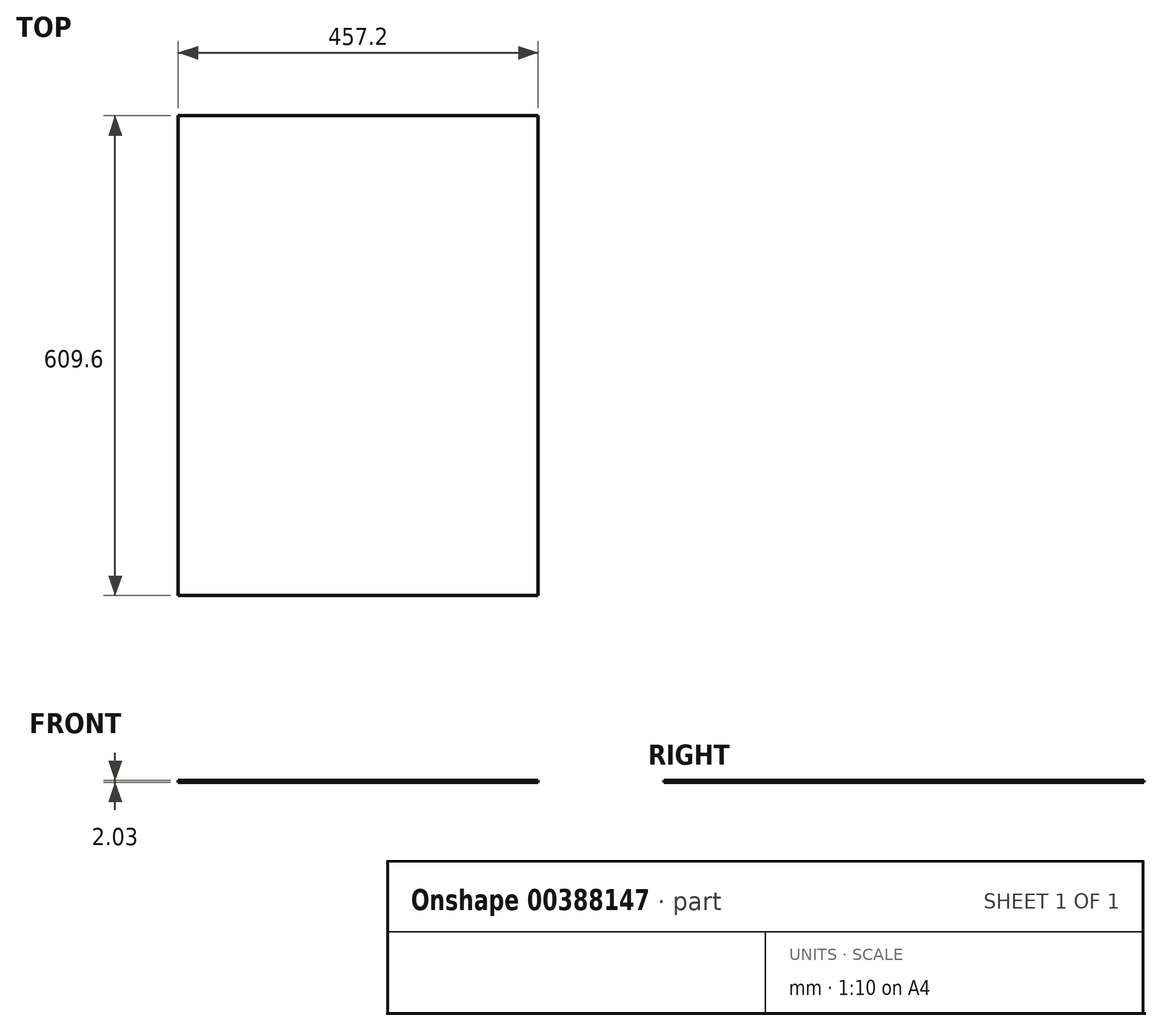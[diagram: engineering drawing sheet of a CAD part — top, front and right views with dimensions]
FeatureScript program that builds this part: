
annotation { "Feature Type Name" : "Feature", "Feature Type Description" : "" }
export const myFeature = defineFeature(function(context is Context, id is Id, definition is map)
    precondition{}
    {
        {
            var Q0;
            Q0=qCreatedBy(makeId("Top.planeOp"),FACE);
            var sketch = newSketch(context, id + "F0", { "sketchPlane" : qUnion([Q0])});
            skLineSegment(sketch, "E0.bottom", {"start": v(228.6, -304.8) * mm, "end": v(-228.6, -304.8) * mm});
            skLineSegment(sketch, "E0.top", {"start": v(228.6, 304.8) * mm, "end": v(-228.6, 304.8) * mm});
            skLineSegment(sketch, "E0.left", {"start": v(228.6, -304.8) * mm, "end": v(228.6, 304.8) * mm});
            skLineSegment(sketch, "E0.right", {"start": v(-228.6, -304.8) * mm, "end": v(-228.6, 304.8) * mm});
            skPoint(sketch, "E0.middle", {"position": v(0, 0) * mm});
            skLineSegment(sketch, "E1", {"start": v(228.6, 120.65) * mm, "end": v(-228.6, 120.65) * mm, "construction": true});
            skLineSegment(sketch, "E2", {"start": v(-228.6, -31.75) * mm, "end": v(228.6, -31.75) * mm, "construction": true});
            skSolve(sketch);
        }
        {
            var Q0;
            Q0 = qSketchRegion(id + "F0", true);
            extrude(context, id + "F1", {"entities" : qUnion([Q0]), "depth" : 2.03 * mm});
        }
    });
